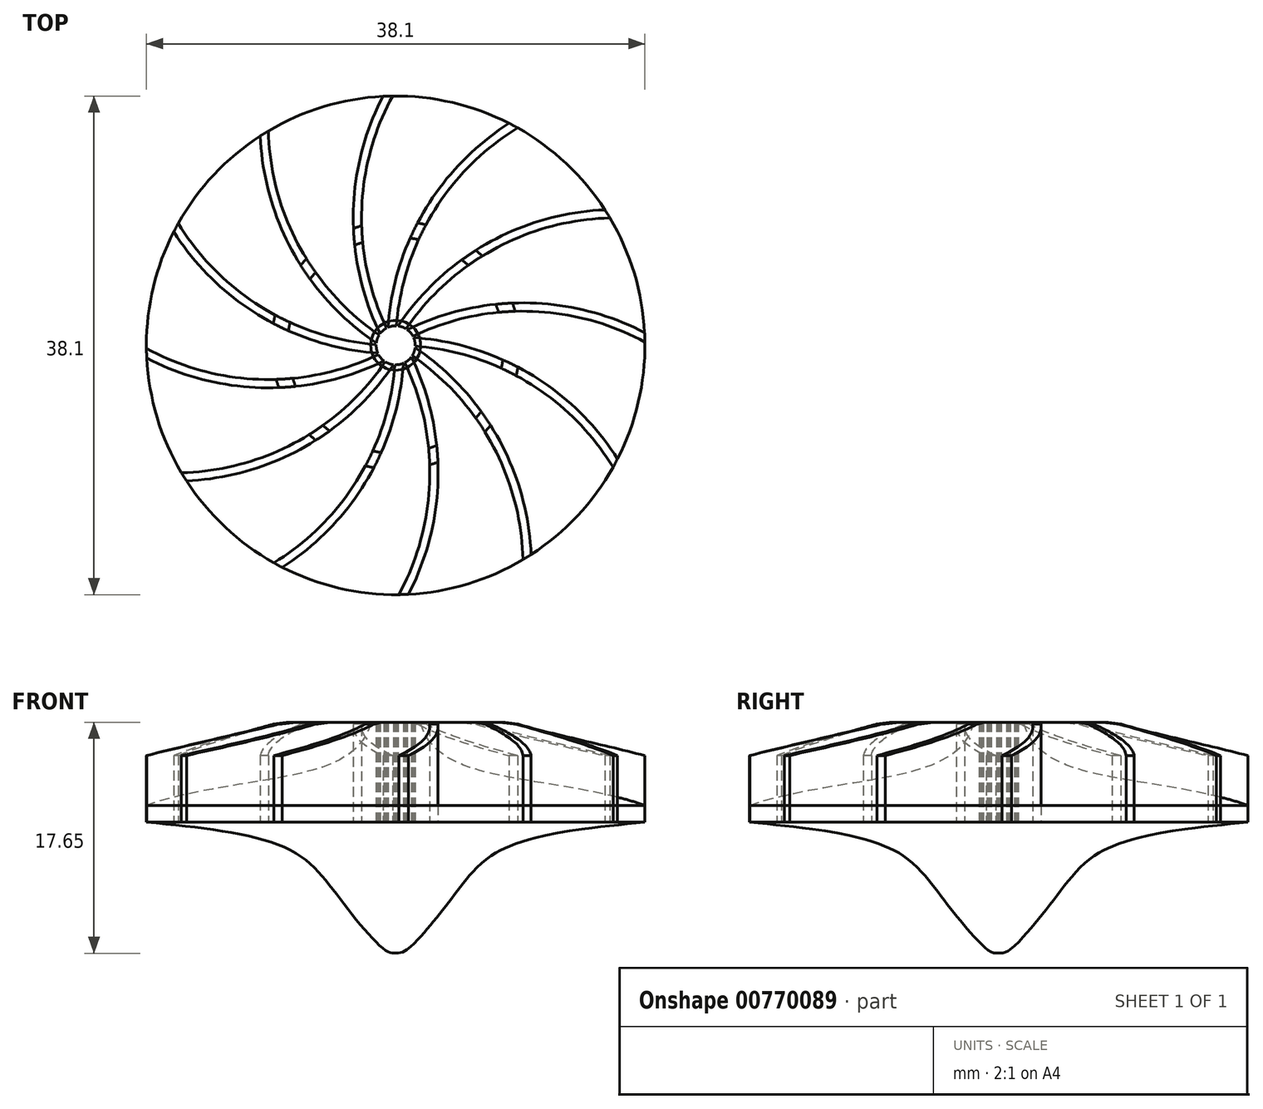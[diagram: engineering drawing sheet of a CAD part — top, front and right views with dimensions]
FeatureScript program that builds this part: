
annotation { "Feature Type Name" : "Feature", "Feature Type Description" : "" }
export const myFeature = defineFeature(function(context is Context, id is Id, definition is map)
    precondition{}
    {
        {
            var Q0;
            Q0=qCreatedBy(makeId("Top.planeOp"),FACE);
            var sketch = newSketch(context, id + "F0", { "sketchPlane" : qUnion([Q0])});
            skCircle(sketch, "E0", {"center": v(0, 0) * mm, "radius": 19.05 * mm});
            skPoint(sketch, "E1", {"position": v(-0.24, 19.05) * mm});
            skPoint(sketch, "E2.1.0", {"position": v(-9.73, 16.38) * mm});
            skPoint(sketch, "E2.2.0", {"position": v(-16.62, 9.32) * mm});
            skPoint(sketch, "E3.0.3.0", {"position": v(-19.05, -0.24) * mm});
            skPoint(sketch, "E3.0.4.0", {"position": v(-16.38, -9.73) * mm});
            skPoint(sketch, "E3.0.5.0", {"position": v(-9.32, -16.62) * mm});
            skPoint(sketch, "E3.0.6.0", {"position": v(0.24, -19.05) * mm});
            skPoint(sketch, "E3.0.7.0", {"position": v(9.73, -16.38) * mm});
            skPoint(sketch, "E3.0.8.0", {"position": v(16.62, -9.32) * mm});
            skPoint(sketch, "E3.0.9.0", {"position": v(19.05, 0.24) * mm});
            skPoint(sketch, "E3.0.10.0", {"position": v(16.38, 9.73) * mm});
            skPoint(sketch, "E3.0.11.0", {"position": v(9.32, 16.62) * mm});
            skArc(sketch, "E4", {"start": v(9.32, 16.62) * mm, "mid": v(2.49, 9.53) * mm, "end": v(0, 0) * mm});
            skArc(sketch, "E5.0", {"start": v(8.67, 16.96) * mm, "mid": v(1.84, 9.67) * mm, "end": v(-0.63, 0) * mm});
            skArc(sketch, "E6.1.0", {"start": v(-0.24, 19.05) * mm, "mid": v(-2.6, 9.5) * mm, "end": v(0, 0) * mm});
            skArc(sketch, "E6.1.1", {"start": v(-0.97, 19.03) * mm, "mid": v(-3.24, 9.3) * mm, "end": v(-0.55, -0.32) * mm});
            skArc(sketch, "E6.2.0", {"start": v(-9.73, 16.38) * mm, "mid": v(-7, 6.92) * mm, "end": v(0, 0) * mm});
            skArc(sketch, "E6.2.1", {"start": v(-10.35, 16) * mm, "mid": v(-7.46, 6.43) * mm, "end": v(-0.32, -0.55) * mm});
            skArc(sketch, "E6.3.0", {"start": v(-16.62, 9.32) * mm, "mid": v(-9.53, 2.49) * mm, "end": v(0, 0) * mm});
            skArc(sketch, "E6.3.1", {"start": v(-16.96, 8.67) * mm, "mid": v(-9.67, 1.84) * mm, "end": v(0, -0.63) * mm});
            skArc(sketch, "E6.4.0", {"start": v(-19.05, -0.24) * mm, "mid": v(-9.5, -2.6) * mm, "end": v(0, 0) * mm});
            skArc(sketch, "E6.4.1", {"start": v(-19.03, -0.97) * mm, "mid": v(-9.3, -3.24) * mm, "end": v(0.32, -0.55) * mm});
            skArc(sketch, "E6.5.0", {"start": v(-16.38, -9.73) * mm, "mid": v(-6.92, -7) * mm, "end": v(0, 0) * mm});
            skArc(sketch, "E6.5.1", {"start": v(-16, -10.35) * mm, "mid": v(-6.43, -7.46) * mm, "end": v(0.55, -0.32) * mm});
            skArc(sketch, "E6.6.0", {"start": v(-9.32, -16.62) * mm, "mid": v(-2.49, -9.53) * mm, "end": v(0, 0) * mm});
            skArc(sketch, "E6.6.1", {"start": v(-8.67, -16.96) * mm, "mid": v(-1.84, -9.67) * mm, "end": v(0.63, 0) * mm});
            skArc(sketch, "E6.7.0", {"start": v(0.24, -19.05) * mm, "mid": v(2.6, -9.5) * mm, "end": v(0, 0) * mm});
            skArc(sketch, "E6.7.1", {"start": v(0.97, -19.03) * mm, "mid": v(3.24, -9.3) * mm, "end": v(0.55, 0.32) * mm});
            skArc(sketch, "E6.8.0", {"start": v(9.73, -16.38) * mm, "mid": v(7, -6.92) * mm, "end": v(0, 0) * mm});
            skArc(sketch, "E6.8.1", {"start": v(10.35, -16) * mm, "mid": v(7.46, -6.43) * mm, "end": v(0.32, 0.55) * mm});
            skArc(sketch, "E6.9.0", {"start": v(16.62, -9.32) * mm, "mid": v(9.53, -2.49) * mm, "end": v(0, 0) * mm});
            skArc(sketch, "E6.9.1", {"start": v(16.96, -8.67) * mm, "mid": v(9.67, -1.84) * mm, "end": v(0, 0.63) * mm});
            skArc(sketch, "E6.10.0", {"start": v(19.05, 0.24) * mm, "mid": v(9.5, 2.6) * mm, "end": v(0, 0) * mm});
            skArc(sketch, "E6.10.1", {"start": v(19.03, 0.97) * mm, "mid": v(9.3, 3.24) * mm, "end": v(-0.32, 0.55) * mm});
            skArc(sketch, "E6.11.0", {"start": v(16.38, 9.73) * mm, "mid": v(6.92, 7) * mm, "end": v(0, 0) * mm});
            skArc(sketch, "E6.11.1", {"start": v(16, 10.35) * mm, "mid": v(6.43, 7.46) * mm, "end": v(-0.55, 0.32) * mm});
            skCircle(sketch, "E7", {"center": v(0, 0) * mm, "radius": 1.5 * mm});
            skSolve(sketch);
        }
        {
            var Q0;
            Q0=qCreatedBy(makeId("Top.planeOp"),FACE);
            var sketch = newSketch(context, id + "F1", { "sketchPlane" : qUnion([Q0])});
            skCircle(sketch, "E8", {"center": v(0, 0) * mm, "radius": 19.05 * mm});
            skSolve(sketch);
        }
        {
            var Q0;
            Q0=qSketchRegion(id+"F1",true);
            extrude(context, id + "F2", {"entities" : qUnion([Q0]), "depth" : 6.35 * mm, "offsetDistance" : 25.4 * mm, "hasSecondDirection" : true, "secondDirectionOppositeDirection" : true, "secondDirectionDepth" : 1.27 * mm});
        }
        {
            var Q0;
            Q0=qCreatedBy(makeId("Front.planeOp"),FACE);
            var sketch = newSketch(context, id + "F3", { "sketchPlane" : qUnion([Q0])});
            skLineSegment(sketch, "E9.bottom", {"start": v(19.05, 6.35) * mm, "end": v(-19.05, 6.35) * mm});
            skLineSegment(sketch, "E9.left", {"start": v(19.05, 6.35) * mm, "end": v(19.05, -5.08) * mm});
            skLineSegment(sketch, "E9.right", {"start": v(-19.05, 6.35) * mm, "end": v(-19.05, -5.08) * mm});
            skPoint(sketch, "E9.middle", {"position": v(0, 0) * mm});
            skLineSegment(sketch, "E10", {"start": v(-19.05, -5.08) * mm, "end": v(19.05, -5.08) * mm});
            skLineSegment(sketch, "E11", {"start": v(-19.05, 0) * mm, "end": v(19.05, 0) * mm, "construction": true});
            skLineSegment(sketch, "E12", {"start": v(0, -5.08) * mm, "end": v(0, 6.35) * mm, "construction": true});
            skPoint(sketch, "E13", {"position": v(1.9, 6.35) * mm});
            skPoint(sketch, "E14", {"position": v(19.05, 1.27) * mm});
            skFitSpline(sketch, "E15", {"points": [v(1.9, 6.35) * mm, v(5.08, 3.11) * mm, v(19.05, 0) * mm, v(28.85, -6.98) * mm], "startDerivative": vector(3.87, -17.8) * mm, "endDerivative": vector(21.57, -22.67) * mm});
            skLineSegment(sketch, "E16", {"start": v(1.9, 6.35) * mm, "end": v(19.05, 6.35) * mm});
            skFitSpline(sketch, "E17", {"points": [v(19.05, -1.28) * mm, v(4.25, -2.54) * mm, v(2.03, -3.42) * mm, v(0.5, -4.83) * mm], "startDerivative": vector(-41.63, 0) * mm, "endDerivative": vector(-3.76, -8.36) * mm});
            skArc(sketch, "E18", {"start": v(0.13, -5.08) * mm, "mid": v(0.4, -4.87) * mm, "end": v(0.64, -4.6) * mm});
            skLineSegment(sketch, "E19", {"start": v(0, -5.08) * mm, "end": v(0, -1.28) * mm});
            skLineSegment(sketch, "E20", {"start": v(0, -1.28) * mm, "end": v(19.05, -1.28) * mm});
            skFitSpline(sketch, "E21", {"points": [v(-19.05, -1.28) * mm, v(-8.03, -3.42) * mm, v(-4.15, -7.28) * mm, v(-0.65, -11.16) * mm, v(0, -11.29) * mm], "startDerivative": vector(33.48, -3.33) * mm, "endDerivative": vector(6, 0.52) * mm});
            skLineSegment(sketch, "E22", {"start": v(0, -11.29) * mm, "end": v(0, -5.08) * mm});
            skLineSegment(sketch, "E23", {"start": v(-19.05, -1.28) * mm, "end": v(0, -1.28) * mm});
            skSolve(sketch);
        }
        {
            var Q0;
            {var subQ2=sQuery(id+"F3.wireOp",EDGE,"E15");Q0=makeQuery(id+"F3.imprint","IMPRINT",FACE,{"disambiguationData":[TD([[makeQuery(id+"F3.imprint","IMPRINT",EDGE,{"derivedFrom":subQ2}),1.0]])]});}
            var Q1;
            Q1=sQuery(id+"F3.wireOp",EDGE,"E12");
            revolve(context, id + "F4", {"operationType" : NewBodyOperationType.REMOVE, "surfaceOperationType" : NewSurfaceOperationType.NEW, "entities" : qUnion([Q0]), "axis" : qUnion([Q1]), "revolveType" : RevolveType.FULL});
        }
        {
            var Q0;
            {var subQ0=sQuery(id+"F0.wireOp",EDGE,"E6.4.0");var subQ1=sQuery(id+"F0.wireOp",EDGE,"E0");var subQ2=makeQuery(id+"F0.imprint","INTERSECT",VERTEX,{"derivedFrom":[subQ1,subQ0]});Q0=makeQuery(id+"F0.imprint","IMPRINT",FACE,{"disambiguationData":[TD([[makeQuery(id+"F0.imprint","IMPRINT",EDGE,{"disambiguationData":[TD([[subQ2,-1.0]])],"derivedFrom":subQ1}),1.0]])]});}
            var Q1;
            {var subQ0=sQuery(id+"F0.wireOp",EDGE,"E6.9.0");var subQ1=sQuery(id+"F0.wireOp",EDGE,"E0");var subQ2=makeQuery(id+"F0.imprint","INTERSECT",VERTEX,{"derivedFrom":[subQ1,subQ0]});Q1=makeQuery(id+"F0.imprint","IMPRINT",FACE,{"disambiguationData":[TD([[makeQuery(id+"F0.imprint","IMPRINT",EDGE,{"disambiguationData":[TD([[subQ2,-1.0]])],"derivedFrom":subQ1}),1.0]])]});}
            var Q2;
            {var subQ0=sQuery(id+"F0.wireOp",EDGE,"E6.6.0");var subQ1=sQuery(id+"F0.wireOp",EDGE,"E0");var subQ2=makeQuery(id+"F0.imprint","INTERSECT",VERTEX,{"derivedFrom":[subQ1,subQ0]});Q2=makeQuery(id+"F0.imprint","IMPRINT",FACE,{"disambiguationData":[TD([[makeQuery(id+"F0.imprint","IMPRINT",EDGE,{"disambiguationData":[TD([[subQ2,-1.0]])],"derivedFrom":subQ1}),1.0]])]});}
            var Q3;
            {var subQ0=sQuery(id+"F0.wireOp",EDGE,"E6.10.0");var subQ1=sQuery(id+"F0.wireOp",EDGE,"E0");var subQ2=makeQuery(id+"F0.imprint","INTERSECT",VERTEX,{"derivedFrom":[subQ1,subQ0]});Q3=makeQuery(id+"F0.imprint","IMPRINT",FACE,{"disambiguationData":[TD([[makeQuery(id+"F0.imprint","IMPRINT",EDGE,{"disambiguationData":[TD([[subQ2,-1.0]])],"derivedFrom":subQ1}),1.0]])]});}
            var Q4;
            {var subQ0=sQuery(id+"F0.wireOp",EDGE,"E6.3.0");var subQ1=sQuery(id+"F0.wireOp",EDGE,"E0");var subQ2=makeQuery(id+"F0.imprint","INTERSECT",VERTEX,{"derivedFrom":[subQ1,subQ0]});Q4=makeQuery(id+"F0.imprint","IMPRINT",FACE,{"disambiguationData":[TD([[makeQuery(id+"F0.imprint","IMPRINT",EDGE,{"disambiguationData":[TD([[subQ2,-1.0]])],"derivedFrom":subQ1}),1.0]])]});}
            var Q5;
            {var subQ0=sQuery(id+"F0.wireOp",EDGE,"E6.8.0");var subQ1=sQuery(id+"F0.wireOp",EDGE,"E0");var subQ2=makeQuery(id+"F0.imprint","INTERSECT",VERTEX,{"derivedFrom":[subQ1,subQ0]});Q5=makeQuery(id+"F0.imprint","IMPRINT",FACE,{"disambiguationData":[TD([[makeQuery(id+"F0.imprint","IMPRINT",EDGE,{"disambiguationData":[TD([[subQ2,-1.0]])],"derivedFrom":subQ1}),1.0]])]});}
            var Q6;
            {var subQ0=sQuery(id+"F0.wireOp",EDGE,"E6.7.0");var subQ1=sQuery(id+"F0.wireOp",EDGE,"E0");var subQ2=makeQuery(id+"F0.imprint","INTERSECT",VERTEX,{"derivedFrom":[subQ1,subQ0]});Q6=makeQuery(id+"F0.imprint","IMPRINT",FACE,{"disambiguationData":[TD([[makeQuery(id+"F0.imprint","IMPRINT",EDGE,{"disambiguationData":[TD([[subQ2,-1.0]])],"derivedFrom":subQ1}),1.0]])]});}
            var Q7;
            {var subQ0=sQuery(id+"F0.wireOp",EDGE,"E6.11.0");var subQ1=sQuery(id+"F0.wireOp",EDGE,"E0");var subQ2=makeQuery(id+"F0.imprint","INTERSECT",VERTEX,{"derivedFrom":[subQ1,subQ0]});Q7=makeQuery(id+"F0.imprint","IMPRINT",FACE,{"disambiguationData":[TD([[makeQuery(id+"F0.imprint","IMPRINT",EDGE,{"disambiguationData":[TD([[subQ2,-1.0]])],"derivedFrom":subQ1}),1.0]])]});}
            var Q8;
            {var subQ0=sQuery(id+"F0.wireOp",EDGE,"E6.1.0");var subQ1=sQuery(id+"F0.wireOp",EDGE,"E0");var subQ2=makeQuery(id+"F0.imprint","INTERSECT",VERTEX,{"derivedFrom":[subQ1,subQ0]});Q8=makeQuery(id+"F0.imprint","IMPRINT",FACE,{"disambiguationData":[TD([[makeQuery(id+"F0.imprint","IMPRINT",EDGE,{"disambiguationData":[TD([[subQ2,-1.0]])],"derivedFrom":subQ1}),1.0]])]});}
            var Q9;
            {var subQ0=sQuery(id+"F0.wireOp",EDGE,"E6.5.0");var subQ1=sQuery(id+"F0.wireOp",EDGE,"E0");var subQ2=makeQuery(id+"F0.imprint","INTERSECT",VERTEX,{"derivedFrom":[subQ1,subQ0]});Q9=makeQuery(id+"F0.imprint","IMPRINT",FACE,{"disambiguationData":[TD([[makeQuery(id+"F0.imprint","IMPRINT",EDGE,{"disambiguationData":[TD([[subQ2,-1.0]])],"derivedFrom":subQ1}),1.0]])]});}
            var Q10;
            {var subQ0=sQuery(id+"F0.wireOp",EDGE,"E4");var subQ1=sQuery(id+"F0.wireOp",EDGE,"E0");var subQ2=makeQuery(id+"F0.imprint","INTERSECT",VERTEX,{"derivedFrom":[subQ1,subQ0]});Q10=makeQuery(id+"F0.imprint","IMPRINT",FACE,{"disambiguationData":[TD([[makeQuery(id+"F0.imprint","IMPRINT",EDGE,{"disambiguationData":[TD([[subQ2,-1.0]])],"derivedFrom":subQ1}),1.0]])]});}
            var Q11;
            {var subQ0=sQuery(id+"F0.wireOp",EDGE,"E6.2.0");var subQ1=sQuery(id+"F0.wireOp",EDGE,"E0");var subQ2=makeQuery(id+"F0.imprint","INTERSECT",VERTEX,{"derivedFrom":[subQ1,subQ0]});Q11=makeQuery(id+"F0.imprint","IMPRINT",FACE,{"disambiguationData":[TD([[makeQuery(id+"F0.imprint","IMPRINT",EDGE,{"disambiguationData":[TD([[subQ2,-1.0]])],"derivedFrom":subQ1}),1.0]])]});}
            extrude(context, id + "F5", {"entities" : qUnion([Q0, Q1, Q2, Q3, Q4, Q5, Q6, Q7, Q8, Q9, Q10, Q11]), "depth" : 6.35 * mm, "offsetDistance" : 25.4 * mm, "hasSecondDirection" : true, "secondDirectionOppositeDirection" : true, "secondDirectionDepth" : 1.27 * mm});
        }
        {
            var Q0;
            {var subQ0=sQuery(id+"F0.wireOp",EDGE,"E0");Q0=makeQuery(id+"F5.opExtrude","CAP_EDGE",EDGE,{"disambiguationData":[OSD([subQ0]),TDD([makeQuery(id+"F0.imprint","IMPRINT",EDGE,{"disambiguationData":[TD([[makeQuery(id+"F0.imprint","INTERSECT",VERTEX,{"derivedFrom":[subQ0,sQuery(id+"F0.wireOp",EDGE,"E6.8.0")]}),-1.0]])],"derivedFrom":subQ0})])],"isStart":false});}
            var Q1;
            {var subQ0=sQuery(id+"F0.wireOp",EDGE,"E0");Q1=makeQuery(id+"F5.opExtrude","CAP_EDGE",EDGE,{"disambiguationData":[OSD([subQ0]),TDD([makeQuery(id+"F0.imprint","IMPRINT",EDGE,{"disambiguationData":[TD([[makeQuery(id+"F0.imprint","INTERSECT",VERTEX,{"derivedFrom":[subQ0,sQuery(id+"F0.wireOp",EDGE,"E6.7.0")]}),-1.0]])],"derivedFrom":subQ0})])],"isStart":false});}
            var Q2;
            {var subQ0=sQuery(id+"F0.wireOp",EDGE,"E0");Q2=makeQuery(id+"F5.opExtrude","CAP_EDGE",EDGE,{"disambiguationData":[OSD([subQ0]),TDD([makeQuery(id+"F0.imprint","IMPRINT",EDGE,{"disambiguationData":[TD([[makeQuery(id+"F0.imprint","INTERSECT",VERTEX,{"derivedFrom":[subQ0,sQuery(id+"F0.wireOp",EDGE,"E6.6.0")]}),-1.0]])],"derivedFrom":subQ0})])],"isStart":false});}
            var Q3;
            {var subQ0=sQuery(id+"F0.wireOp",EDGE,"E0");Q3=makeQuery(id+"F5.opExtrude","CAP_EDGE",EDGE,{"disambiguationData":[OSD([subQ0]),TDD([makeQuery(id+"F0.imprint","IMPRINT",EDGE,{"disambiguationData":[TD([[makeQuery(id+"F0.imprint","INTERSECT",VERTEX,{"derivedFrom":[subQ0,sQuery(id+"F0.wireOp",EDGE,"E6.5.0")]}),-1.0]])],"derivedFrom":subQ0})])],"isStart":false});}
            var Q4;
            {var subQ0=sQuery(id+"F0.wireOp",EDGE,"E0");Q4=makeQuery(id+"F5.opExtrude","CAP_EDGE",EDGE,{"disambiguationData":[OSD([subQ0]),TDD([makeQuery(id+"F0.imprint","IMPRINT",EDGE,{"disambiguationData":[TD([[makeQuery(id+"F0.imprint","INTERSECT",VERTEX,{"derivedFrom":[subQ0,sQuery(id+"F0.wireOp",EDGE,"E6.4.0")]}),-1.0]])],"derivedFrom":subQ0})])],"isStart":false});}
            var Q5;
            {var subQ0=sQuery(id+"F0.wireOp",EDGE,"E0");Q5=makeQuery(id+"F5.opExtrude","CAP_EDGE",EDGE,{"disambiguationData":[OSD([subQ0]),TDD([makeQuery(id+"F0.imprint","IMPRINT",EDGE,{"disambiguationData":[TD([[makeQuery(id+"F0.imprint","INTERSECT",VERTEX,{"derivedFrom":[subQ0,sQuery(id+"F0.wireOp",EDGE,"E6.3.0")]}),-1.0]])],"derivedFrom":subQ0})])],"isStart":false});}
            var Q6;
            {var subQ0=sQuery(id+"F0.wireOp",EDGE,"E0");Q6=makeQuery(id+"F5.opExtrude","CAP_EDGE",EDGE,{"disambiguationData":[OSD([subQ0]),TDD([makeQuery(id+"F0.imprint","IMPRINT",EDGE,{"disambiguationData":[TD([[makeQuery(id+"F0.imprint","INTERSECT",VERTEX,{"derivedFrom":[subQ0,sQuery(id+"F0.wireOp",EDGE,"E6.2.0")]}),-1.0]])],"derivedFrom":subQ0})])],"isStart":false});}
            var Q7;
            {var subQ0=sQuery(id+"F0.wireOp",EDGE,"E0");Q7=makeQuery(id+"F5.opExtrude","CAP_EDGE",EDGE,{"disambiguationData":[OSD([subQ0]),TDD([makeQuery(id+"F0.imprint","IMPRINT",EDGE,{"disambiguationData":[TD([[makeQuery(id+"F0.imprint","INTERSECT",VERTEX,{"derivedFrom":[subQ0,sQuery(id+"F0.wireOp",EDGE,"E6.1.0")]}),-1.0]])],"derivedFrom":subQ0})])],"isStart":false});}
            var Q8;
            {var subQ0=sQuery(id+"F0.wireOp",EDGE,"E0");Q8=makeQuery(id+"F5.opExtrude","CAP_EDGE",EDGE,{"disambiguationData":[OSD([subQ0]),TDD([makeQuery(id+"F0.imprint","IMPRINT",EDGE,{"disambiguationData":[TD([[makeQuery(id+"F0.imprint","INTERSECT",VERTEX,{"derivedFrom":[subQ0,sQuery(id+"F0.wireOp",EDGE,"E4")]}),-1.0]])],"derivedFrom":subQ0})])],"isStart":false});}
            var Q9;
            {var subQ0=sQuery(id+"F0.wireOp",EDGE,"E0");Q9=makeQuery(id+"F5.opExtrude","CAP_EDGE",EDGE,{"disambiguationData":[OSD([subQ0]),TDD([makeQuery(id+"F0.imprint","IMPRINT",EDGE,{"disambiguationData":[TD([[makeQuery(id+"F0.imprint","INTERSECT",VERTEX,{"derivedFrom":[subQ0,sQuery(id+"F0.wireOp",EDGE,"E6.11.0")]}),-1.0]])],"derivedFrom":subQ0})])],"isStart":false});}
            var Q10;
            {var subQ0=sQuery(id+"F0.wireOp",EDGE,"E0");Q10=makeQuery(id+"F5.opExtrude","CAP_EDGE",EDGE,{"disambiguationData":[OSD([subQ0]),TDD([makeQuery(id+"F0.imprint","IMPRINT",EDGE,{"disambiguationData":[TD([[makeQuery(id+"F0.imprint","INTERSECT",VERTEX,{"derivedFrom":[subQ0,sQuery(id+"F0.wireOp",EDGE,"E6.10.0")]}),-1.0]])],"derivedFrom":subQ0})])],"isStart":false});}
            var Q11;
            {var subQ0=sQuery(id+"F0.wireOp",EDGE,"E0");Q11=makeQuery(id+"F5.opExtrude","CAP_EDGE",EDGE,{"disambiguationData":[OSD([subQ0]),TDD([makeQuery(id+"F0.imprint","IMPRINT",EDGE,{"disambiguationData":[TD([[makeQuery(id+"F0.imprint","INTERSECT",VERTEX,{"derivedFrom":[subQ0,sQuery(id+"F0.wireOp",EDGE,"E6.9.0")]}),-1.0]])],"derivedFrom":subQ0})])],"isStart":false});}
            chamfer(context, id + "F6", {"entities" : qUnion([Q0, Q1, Q2, Q3, Q4, Q5, Q6, Q7, Q8, Q9, Q10, Q11]), "chamferType" : ChamferType.TWO_OFFSETS, "width1" : 10.16 * mm, "oppositeDirection" : false, "width2" : 2.54 * mm, "tangentPropagation" : true});
        }
        {
            var Q0;
            {var subQ0=sQuery(id+"F0.wireOp",EDGE,"E6.8.1");var subQ1=sQuery(id+"F0.wireOp",EDGE,"E6.8.0");var subQ2=sQuery(id+"F0.wireOp",EDGE,"E0");Q0=makeQuery(id+"F6.opChamfer","BLEND_EDGE",EDGE,{"blendedFrom":[makeQuery(id+"F5.opExtrude","CAP_EDGE",EDGE,{"disambiguationData":[OSD([subQ2]),TDD([makeQuery(id+"F0.imprint","IMPRINT",EDGE,{"disambiguationData":[TD([[makeQuery(id+"F0.imprint","INTERSECT",VERTEX,{"derivedFrom":[subQ2,subQ1]}),-1.0]])],"derivedFrom":subQ2})])],"isStart":false}),makeQuery(id+"F5.opExtrude","CAP_FACE",FACE,{"disambiguationData":[OSD([subQ2,subQ1,subQ0,sQuery(id+"F0.wireOp",EDGE,"E7")])],"isStart":false})],"blendedInto":[makeQuery(id+"F5.opExtrude","CAP_FACE",FACE,{"disambiguationData":[OSD([subQ2,subQ1,subQ0,sQuery(id+"F0.wireOp",EDGE,"E7")])],"isStart":false})]});}
            var Q1;
            {var subQ0=sQuery(id+"F0.wireOp",EDGE,"E6.7.1");var subQ1=sQuery(id+"F0.wireOp",EDGE,"E6.7.0");var subQ2=sQuery(id+"F0.wireOp",EDGE,"E0");Q1=makeQuery(id+"F6.opChamfer","BLEND_EDGE",EDGE,{"blendedFrom":[makeQuery(id+"F5.opExtrude","CAP_EDGE",EDGE,{"disambiguationData":[OSD([subQ2]),TDD([makeQuery(id+"F0.imprint","IMPRINT",EDGE,{"disambiguationData":[TD([[makeQuery(id+"F0.imprint","INTERSECT",VERTEX,{"derivedFrom":[subQ2,subQ1]}),-1.0]])],"derivedFrom":subQ2})])],"isStart":false}),makeQuery(id+"F5.opExtrude","CAP_FACE",FACE,{"disambiguationData":[OSD([subQ2,subQ1,subQ0,sQuery(id+"F0.wireOp",EDGE,"E7")])],"isStart":false})],"blendedInto":[makeQuery(id+"F5.opExtrude","CAP_FACE",FACE,{"disambiguationData":[OSD([subQ2,subQ1,subQ0,sQuery(id+"F0.wireOp",EDGE,"E7")])],"isStart":false})]});}
            var Q2;
            {var subQ0=sQuery(id+"F0.wireOp",EDGE,"E6.9.1");var subQ1=sQuery(id+"F0.wireOp",EDGE,"E6.9.0");var subQ2=sQuery(id+"F0.wireOp",EDGE,"E0");Q2=makeQuery(id+"F6.opChamfer","BLEND_EDGE",EDGE,{"blendedFrom":[makeQuery(id+"F5.opExtrude","CAP_EDGE",EDGE,{"disambiguationData":[OSD([subQ2]),TDD([makeQuery(id+"F0.imprint","IMPRINT",EDGE,{"disambiguationData":[TD([[makeQuery(id+"F0.imprint","INTERSECT",VERTEX,{"derivedFrom":[subQ2,subQ1]}),-1.0]])],"derivedFrom":subQ2})])],"isStart":false}),makeQuery(id+"F5.opExtrude","CAP_FACE",FACE,{"disambiguationData":[OSD([subQ2,subQ1,subQ0,sQuery(id+"F0.wireOp",EDGE,"E7")])],"isStart":false})],"blendedInto":[makeQuery(id+"F5.opExtrude","CAP_FACE",FACE,{"disambiguationData":[OSD([subQ2,subQ1,subQ0,sQuery(id+"F0.wireOp",EDGE,"E7")])],"isStart":false})]});}
            var Q3;
            {var subQ0=sQuery(id+"F0.wireOp",EDGE,"E6.10.1");var subQ1=sQuery(id+"F0.wireOp",EDGE,"E6.10.0");var subQ2=sQuery(id+"F0.wireOp",EDGE,"E0");Q3=makeQuery(id+"F6.opChamfer","BLEND_EDGE",EDGE,{"blendedFrom":[makeQuery(id+"F5.opExtrude","CAP_EDGE",EDGE,{"disambiguationData":[OSD([subQ2]),TDD([makeQuery(id+"F0.imprint","IMPRINT",EDGE,{"disambiguationData":[TD([[makeQuery(id+"F0.imprint","INTERSECT",VERTEX,{"derivedFrom":[subQ2,subQ1]}),-1.0]])],"derivedFrom":subQ2})])],"isStart":false}),makeQuery(id+"F5.opExtrude","CAP_FACE",FACE,{"disambiguationData":[OSD([subQ2,subQ1,subQ0,sQuery(id+"F0.wireOp",EDGE,"E7")])],"isStart":false})],"blendedInto":[makeQuery(id+"F5.opExtrude","CAP_FACE",FACE,{"disambiguationData":[OSD([subQ2,subQ1,subQ0,sQuery(id+"F0.wireOp",EDGE,"E7")])],"isStart":false})]});}
            var Q4;
            {var subQ0=sQuery(id+"F0.wireOp",EDGE,"E6.11.1");var subQ1=sQuery(id+"F0.wireOp",EDGE,"E6.11.0");var subQ2=sQuery(id+"F0.wireOp",EDGE,"E0");Q4=makeQuery(id+"F6.opChamfer","BLEND_EDGE",EDGE,{"blendedFrom":[makeQuery(id+"F5.opExtrude","CAP_EDGE",EDGE,{"disambiguationData":[OSD([subQ2]),TDD([makeQuery(id+"F0.imprint","IMPRINT",EDGE,{"disambiguationData":[TD([[makeQuery(id+"F0.imprint","INTERSECT",VERTEX,{"derivedFrom":[subQ2,subQ1]}),-1.0]])],"derivedFrom":subQ2})])],"isStart":false}),makeQuery(id+"F5.opExtrude","CAP_FACE",FACE,{"disambiguationData":[OSD([subQ2,subQ1,subQ0,sQuery(id+"F0.wireOp",EDGE,"E7")])],"isStart":false})],"blendedInto":[makeQuery(id+"F5.opExtrude","CAP_FACE",FACE,{"disambiguationData":[OSD([subQ2,subQ1,subQ0,sQuery(id+"F0.wireOp",EDGE,"E7")])],"isStart":false})]});}
            var Q5;
            {var subQ0=sQuery(id+"F0.wireOp",EDGE,"E5.0");var subQ1=sQuery(id+"F0.wireOp",EDGE,"E4");var subQ2=sQuery(id+"F0.wireOp",EDGE,"E0");Q5=makeQuery(id+"F6.opChamfer","BLEND_EDGE",EDGE,{"blendedFrom":[makeQuery(id+"F5.opExtrude","CAP_EDGE",EDGE,{"disambiguationData":[OSD([subQ2]),TDD([makeQuery(id+"F0.imprint","IMPRINT",EDGE,{"disambiguationData":[TD([[makeQuery(id+"F0.imprint","INTERSECT",VERTEX,{"derivedFrom":[subQ2,subQ1]}),-1.0]])],"derivedFrom":subQ2})])],"isStart":false}),makeQuery(id+"F5.opExtrude","CAP_FACE",FACE,{"disambiguationData":[OSD([subQ2,subQ1,subQ0,sQuery(id+"F0.wireOp",EDGE,"E7")])],"isStart":false})],"blendedInto":[makeQuery(id+"F5.opExtrude","CAP_FACE",FACE,{"disambiguationData":[OSD([subQ2,subQ1,subQ0,sQuery(id+"F0.wireOp",EDGE,"E7")])],"isStart":false})]});}
            var Q6;
            {var subQ0=sQuery(id+"F0.wireOp",EDGE,"E6.1.1");var subQ1=sQuery(id+"F0.wireOp",EDGE,"E6.1.0");var subQ2=sQuery(id+"F0.wireOp",EDGE,"E0");Q6=makeQuery(id+"F6.opChamfer","BLEND_EDGE",EDGE,{"blendedFrom":[makeQuery(id+"F5.opExtrude","CAP_EDGE",EDGE,{"disambiguationData":[OSD([subQ2]),TDD([makeQuery(id+"F0.imprint","IMPRINT",EDGE,{"disambiguationData":[TD([[makeQuery(id+"F0.imprint","INTERSECT",VERTEX,{"derivedFrom":[subQ2,subQ1]}),-1.0]])],"derivedFrom":subQ2})])],"isStart":false}),makeQuery(id+"F5.opExtrude","CAP_FACE",FACE,{"disambiguationData":[OSD([subQ2,subQ1,subQ0,sQuery(id+"F0.wireOp",EDGE,"E7")])],"isStart":false})],"blendedInto":[makeQuery(id+"F5.opExtrude","CAP_FACE",FACE,{"disambiguationData":[OSD([subQ2,subQ1,subQ0,sQuery(id+"F0.wireOp",EDGE,"E7")])],"isStart":false})]});}
            var Q7;
            {var subQ0=sQuery(id+"F0.wireOp",EDGE,"E6.2.1");var subQ1=sQuery(id+"F0.wireOp",EDGE,"E6.2.0");var subQ2=sQuery(id+"F0.wireOp",EDGE,"E0");Q7=makeQuery(id+"F6.opChamfer","BLEND_EDGE",EDGE,{"blendedFrom":[makeQuery(id+"F5.opExtrude","CAP_EDGE",EDGE,{"disambiguationData":[OSD([subQ2]),TDD([makeQuery(id+"F0.imprint","IMPRINT",EDGE,{"disambiguationData":[TD([[makeQuery(id+"F0.imprint","INTERSECT",VERTEX,{"derivedFrom":[subQ2,subQ1]}),-1.0]])],"derivedFrom":subQ2})])],"isStart":false}),makeQuery(id+"F5.opExtrude","CAP_FACE",FACE,{"disambiguationData":[OSD([subQ2,subQ1,subQ0,sQuery(id+"F0.wireOp",EDGE,"E7")])],"isStart":false})],"blendedInto":[makeQuery(id+"F5.opExtrude","CAP_FACE",FACE,{"disambiguationData":[OSD([subQ2,subQ1,subQ0,sQuery(id+"F0.wireOp",EDGE,"E7")])],"isStart":false})]});}
            var Q8;
            {var subQ0=sQuery(id+"F0.wireOp",EDGE,"E6.3.1");var subQ1=sQuery(id+"F0.wireOp",EDGE,"E6.3.0");var subQ2=sQuery(id+"F0.wireOp",EDGE,"E0");Q8=makeQuery(id+"F6.opChamfer","BLEND_EDGE",EDGE,{"blendedFrom":[makeQuery(id+"F5.opExtrude","CAP_EDGE",EDGE,{"disambiguationData":[OSD([subQ2]),TDD([makeQuery(id+"F0.imprint","IMPRINT",EDGE,{"disambiguationData":[TD([[makeQuery(id+"F0.imprint","INTERSECT",VERTEX,{"derivedFrom":[subQ2,subQ1]}),-1.0]])],"derivedFrom":subQ2})])],"isStart":false}),makeQuery(id+"F5.opExtrude","CAP_FACE",FACE,{"disambiguationData":[OSD([subQ2,subQ1,subQ0,sQuery(id+"F0.wireOp",EDGE,"E7")])],"isStart":false})],"blendedInto":[makeQuery(id+"F5.opExtrude","CAP_FACE",FACE,{"disambiguationData":[OSD([subQ2,subQ1,subQ0,sQuery(id+"F0.wireOp",EDGE,"E7")])],"isStart":false})]});}
            var Q9;
            {var subQ0=sQuery(id+"F0.wireOp",EDGE,"E6.4.1");var subQ1=sQuery(id+"F0.wireOp",EDGE,"E6.4.0");var subQ2=sQuery(id+"F0.wireOp",EDGE,"E0");Q9=makeQuery(id+"F6.opChamfer","BLEND_EDGE",EDGE,{"blendedFrom":[makeQuery(id+"F5.opExtrude","CAP_EDGE",EDGE,{"disambiguationData":[OSD([subQ2]),TDD([makeQuery(id+"F0.imprint","IMPRINT",EDGE,{"disambiguationData":[TD([[makeQuery(id+"F0.imprint","INTERSECT",VERTEX,{"derivedFrom":[subQ2,subQ1]}),-1.0]])],"derivedFrom":subQ2})])],"isStart":false}),makeQuery(id+"F5.opExtrude","CAP_FACE",FACE,{"disambiguationData":[OSD([subQ2,subQ1,subQ0,sQuery(id+"F0.wireOp",EDGE,"E7")])],"isStart":false})],"blendedInto":[makeQuery(id+"F5.opExtrude","CAP_FACE",FACE,{"disambiguationData":[OSD([subQ2,subQ1,subQ0,sQuery(id+"F0.wireOp",EDGE,"E7")])],"isStart":false})]});}
            var Q10;
            {var subQ0=sQuery(id+"F0.wireOp",EDGE,"E6.6.1");var subQ1=sQuery(id+"F0.wireOp",EDGE,"E6.6.0");var subQ2=sQuery(id+"F0.wireOp",EDGE,"E0");Q10=makeQuery(id+"F6.opChamfer","BLEND_EDGE",EDGE,{"blendedFrom":[makeQuery(id+"F5.opExtrude","CAP_EDGE",EDGE,{"disambiguationData":[OSD([subQ2]),TDD([makeQuery(id+"F0.imprint","IMPRINT",EDGE,{"disambiguationData":[TD([[makeQuery(id+"F0.imprint","INTERSECT",VERTEX,{"derivedFrom":[subQ2,subQ1]}),-1.0]])],"derivedFrom":subQ2})])],"isStart":false}),makeQuery(id+"F5.opExtrude","CAP_FACE",FACE,{"disambiguationData":[OSD([subQ2,subQ1,subQ0,sQuery(id+"F0.wireOp",EDGE,"E7")])],"isStart":false})],"blendedInto":[makeQuery(id+"F5.opExtrude","CAP_FACE",FACE,{"disambiguationData":[OSD([subQ2,subQ1,subQ0,sQuery(id+"F0.wireOp",EDGE,"E7")])],"isStart":false})]});}
            var Q11;
            {var subQ0=sQuery(id+"F0.wireOp",EDGE,"E6.5.1");var subQ1=sQuery(id+"F0.wireOp",EDGE,"E6.5.0");var subQ2=sQuery(id+"F0.wireOp",EDGE,"E0");Q11=makeQuery(id+"F6.opChamfer","BLEND_EDGE",EDGE,{"blendedFrom":[makeQuery(id+"F5.opExtrude","CAP_EDGE",EDGE,{"disambiguationData":[OSD([subQ2]),TDD([makeQuery(id+"F0.imprint","IMPRINT",EDGE,{"disambiguationData":[TD([[makeQuery(id+"F0.imprint","INTERSECT",VERTEX,{"derivedFrom":[subQ2,subQ1]}),-1.0]])],"derivedFrom":subQ2})])],"isStart":false}),makeQuery(id+"F5.opExtrude","CAP_FACE",FACE,{"disambiguationData":[OSD([subQ2,subQ1,subQ0,sQuery(id+"F0.wireOp",EDGE,"E7")])],"isStart":false})],"blendedInto":[makeQuery(id+"F5.opExtrude","CAP_FACE",FACE,{"disambiguationData":[OSD([subQ2,subQ1,subQ0,sQuery(id+"F0.wireOp",EDGE,"E7")])],"isStart":false})]});}
            chamfer(context, id + "F7", {"entities" : qUnion([Q0, Q1, Q2, Q3, Q4, Q5, Q6, Q7, Q8, Q9, Q10, Q11]), "width" : 5.08 * mm, "tangentPropagation" : true});
        }
        {
            var Q0;
            Q0=makeQuery(id+"F3.imprint","IMPRINT",FACE,{"disambiguationData":[TD([[makeQuery(id+"F3.imprint","IMPRINT",EDGE,{"derivedFrom":sQuery(id+"F3.wireOp",EDGE,"E9.bottom")}),1.0]])]});
            var sketch = newSketch(context, id + "F8", { "sketchPlane" : qUnion([Q0])});
            skLineSegment(sketch, "E24.bottom", {"start": v(-19.05, -4.25) * mm, "end": v(19.05, -4.25) * mm});
            skLineSegment(sketch, "E24.top", {"start": v(-19.05, -1.27) * mm, "end": v(19.05, -1.27) * mm});
            skLineSegment(sketch, "E24.left", {"start": v(-19.05, -4.25) * mm, "end": v(-19.05, -1.27) * mm});
            skLineSegment(sketch, "E24.right", {"start": v(19.05, -4.25) * mm, "end": v(19.05, -1.27) * mm});
            skPoint(sketch, "E25", {"position": v(0, -4.25) * mm});
            skSolve(sketch);
        }
        {
            var Q0;
            {var subQ7=sQuery(id+"F8.wireOp",EDGE,"E24.top");Q0=makeQuery(id+"F8.imprint","IMPRINT",FACE,{"disambiguationData":[TD([[makeQuery(id+"F8.imprint","IMPRINT",EDGE,{"derivedFrom":subQ7}),-1.0]])]});}
            var Q1;
            {var subQ0=sQuery(id+"F8.wireOp",EDGE,"E24.right");var subQ1=sQuery(id+"F8.wireOp",EDGE,"E24.bottom");var subQ2=makeQuery(id+"F8.imprint","INTERSECT",VERTEX,{"derivedFrom":[subQ1,subQ0]});Q1=makeQuery(id+"F8.imprint","IMPRINT",FACE,{"disambiguationData":[TD([[makeQuery(id+"F8.imprint","IMPRINT",EDGE,{"disambiguationData":[TD([[subQ2,1.0]])],"derivedFrom":subQ1}),1.0]])]});}
            extrude(context, id + "F9", {"entities" : qUnion([Q0, Q1]), "operationType" : NewBodyOperationType.REMOVE, "endBound" : BoundingType.SYMMETRIC, "oppositeDirection" : true, "depth" : 127 * mm, "offsetDistance" : 25.4 * mm, "hasSecondDirection" : true, "secondDirectionBound" : SecondDirectionBoundingType.THROUGH_ALL, "secondDirectionOppositeDirection" : false, "secondDirectionDepth" : 25.4 * mm});
        }
        {
            var Q0;
            {var subQ0=sQuery(id+"F3.wireOp",EDGE,"E22");Q0=makeQuery(id+"F3.imprint","IMPRINT",FACE,{"disambiguationData":[TD([[makeQuery(id+"F3.imprint","IMPRINT",EDGE,{"derivedFrom":subQ0}),1.0]])]});}
            var Q1;
            {var subQ0=sQuery(id+"F3.wireOp",EDGE,"E19");Q1=makeQuery(id+"F3.imprint","IMPRINT",FACE,{"disambiguationData":[TD([[makeQuery(id+"F3.imprint","IMPRINT",EDGE,{"derivedFrom":subQ0}),1.0]])]});}
            var Q2;
            Q2=sQuery(id+"F3.wireOp",EDGE,"E12");
            revolve(context, id + "F10", {"surfaceOperationType" : NewSurfaceOperationType.NEW, "entities" : qUnion([Q0, Q1]), "axis" : qUnion([Q2]), "revolveType" : RevolveType.FULL});
        }
    });
